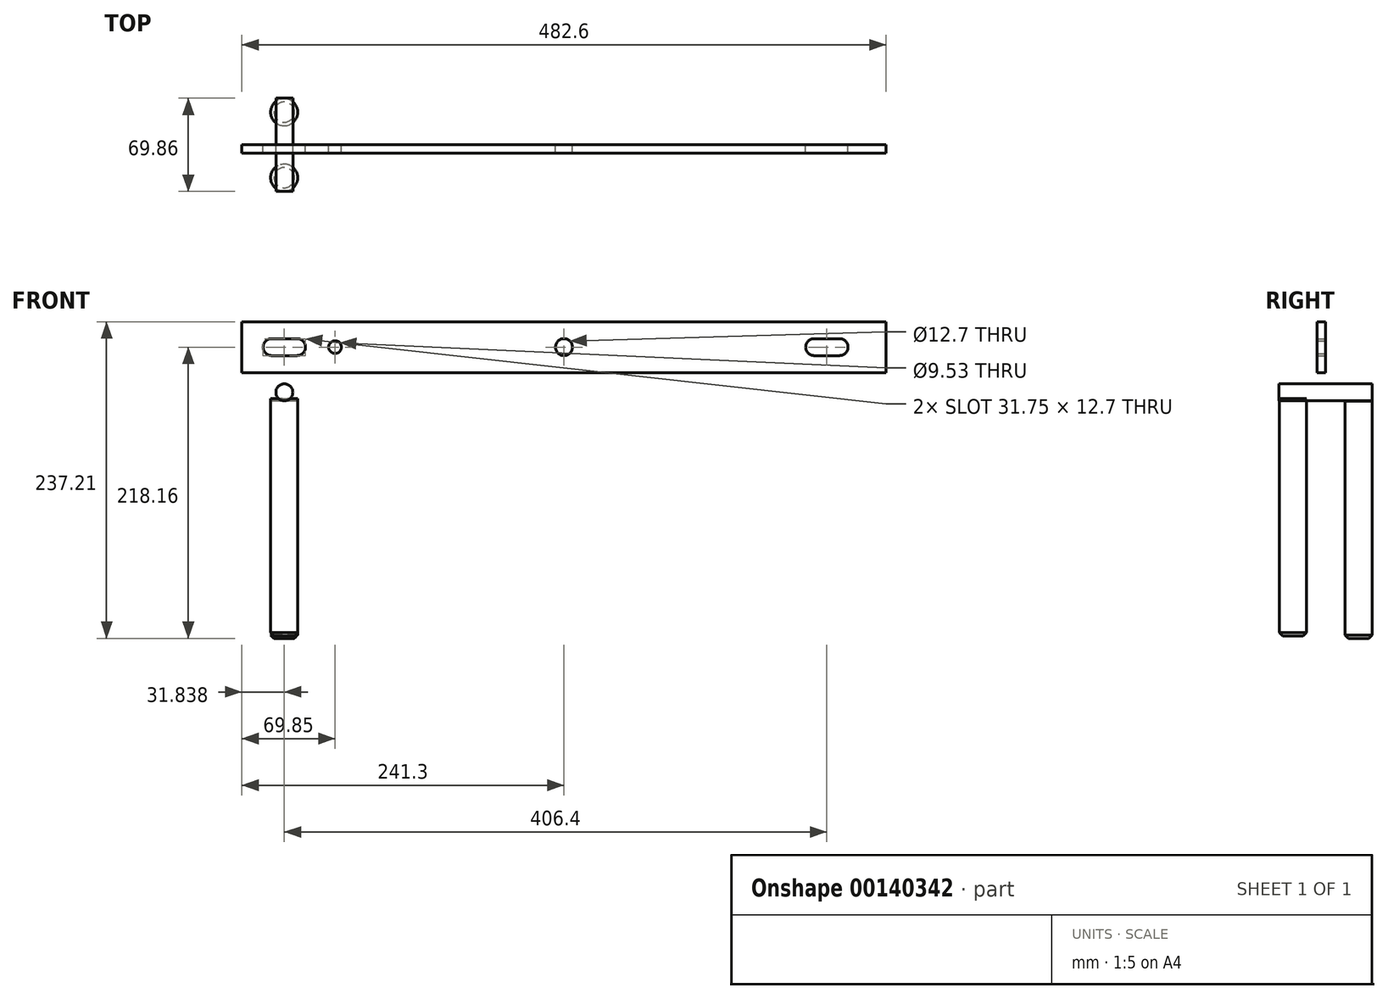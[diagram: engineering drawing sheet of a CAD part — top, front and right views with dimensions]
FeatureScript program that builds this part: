
annotation { "Feature Type Name" : "Feature", "Feature Type Description" : "" }
export const myFeature = defineFeature(function(context is Context, id is Id, definition is map)
    precondition{}
    {
        {
            var Q0;
            Q0=qCreatedBy(makeId("Front.planeOp"),FACE);
            var sketch = newSketch(context, id + "F0", { "sketchPlane" : qUnion([Q0])});
            skLineSegment(sketch, "E0.bottom", {"start": v(-241.3, 19.05) * mm, "end": v(241.3, 19.05) * mm});
            skLineSegment(sketch, "E0.top", {"start": v(-241.3, -19.05) * mm, "end": v(241.3, -19.05) * mm});
            skLineSegment(sketch, "E0.left", {"start": v(-241.3, 19.05) * mm, "end": v(-241.3, -19.05) * mm});
            skLineSegment(sketch, "E0.right", {"start": v(241.3, 19.05) * mm, "end": v(241.3, -19.05) * mm});
            skPoint(sketch, "E0.middle", {"position": v(0, 0) * mm});
            skCircle(sketch, "E1", {"center": v(0, 0) * mm, "radius": 6.35 * mm});
            skCircle(sketch, "E2", {"center": v(-171.45, 0) * mm, "radius": 4.76 * mm});
            skPoint(sketch, "E3", {"position": v(-209.46, 0) * mm});
            skPoint(sketch, "E4", {"position": v(196.94, 0) * mm});
            skPoint(sketch, "E5", {"position": v(-193.59, 0) * mm});
            skPoint(sketch, "E6", {"position": v(-225.34, 0) * mm});
            skPoint(sketch, "E7", {"position": v(212.81, 0) * mm});
            skPoint(sketch, "E8", {"position": v(181.06, 0) * mm});
            skLineSegment(sketch, "E9.bottom", {"start": v(-218.99, 6.35) * mm, "end": v(-199.94, 6.35) * mm});
            skLineSegment(sketch, "E9.top", {"start": v(-218.99, -6.35) * mm, "end": v(-199.94, -6.35) * mm});
            skCircle(sketch, "E10", {"center": v(-218.99, 0) * mm, "radius": 6.35 * mm});
            skCircle(sketch, "E11", {"center": v(-199.94, 0) * mm, "radius": 6.35 * mm});
            skLineSegment(sketch, "E12.bottom", {"start": v(206.46, 6.35) * mm, "end": v(187.41, 6.35) * mm});
            skLineSegment(sketch, "E12.top", {"start": v(206.46, -6.35) * mm, "end": v(187.41, -6.35) * mm});
            skCircle(sketch, "E13", {"center": v(187.41, 0) * mm, "radius": 6.35 * mm});
            skCircle(sketch, "E14", {"center": v(206.46, 0) * mm, "radius": 6.35 * mm});
            skSolve(sketch);
        }
        {
            var Q0;
            Q0=makeQuery(id+"F0.imprint","IMPRINT",FACE,{"disambiguationData":[TD([[makeQuery(id+"F0.imprint","IMPRINT",EDGE,{"derivedFrom":sQuery(id+"F0.wireOp",EDGE,"E0.bottom")}),-1.0]])]});
            extrude(context, id + "F1", {"entities" : qUnion([Q0]), "depth" : 6.35 * mm});
        }
        {
            var Q0;
            Q0=qCreatedBy(makeId("Front.planeOp"),FACE);
            var sketch = newSketch(context, id + "F2", { "sketchPlane" : qUnion([Q0])});
            skCircle(sketch, "E15", {"center": v(-209.45, -33.86) * mm, "radius": 6.35 * mm});
            skSolve(sketch);
        }
        {
            var Q0;
            Q0=makeQuery(id+"F2.imprint","IMPRINT",FACE,{"disambiguationData":[TD([[makeQuery(id+"F2.imprint","IMPRINT",EDGE,{"derivedFrom":sQuery(id+"F2.wireOp",EDGE,"E15")}),1.0]])]});
            extrude(context, id + "F3", {"entities" : qUnion([Q0]), "endBound" : BoundingType.SYMMETRIC, "depth" : 69.85 * mm});
        }
        {
            var Q0;
            Q0=qCreatedBy(makeId("Top.planeOp"),FACE);
            var sketch = newSketch(context, id + "F4", { "sketchPlane" : qUnion([Q0])});
            skLineSegment(sketch, "E16", {"start": v(-209.57, 44.7) * mm, "end": v(-209.57, -47.23) * mm});
            skCircle(sketch, "E17", {"center": v(-209.57, -45.42) * mm, "radius": 10.14 * mm});
            skSolve(sketch);
        }
        {
            var Q0;
            Q0=makeQuery(id+"F4.imprint","IMPRINT",FACE,{"disambiguationData":[TD([[makeQuery(id+"F4.imprint","IMPRINT",EDGE,{"derivedFrom":sQuery(id+"F4.wireOp",EDGE,"E17")}),1.0]])]});
            extrude(context, id + "F5", {"entities" : qUnion([Q0]), "operationType" : NewBodyOperationType.ADD, "oppositeDirection" : true, "depth" : 203.2 * mm, "hasSecondDirection" : true, "secondDirectionOppositeDirection" : true, "secondDirectionDepth" : 25.4 * mm});
        }
        {
            var Q0;
            Q0=makeQuery(id+"F5.opExtrude","SWEPT_BODY",BODY,{"disambiguationData":[OSD([sQuery(id+"F4.wireOp",EDGE,"E17")])]});
            transform(context, id + "F6", {"entities" : qUnion([Q0]), "transformType" : TransformType.TRANSLATION_3D, "dx" : 0 * mm, "dy" : 69.92 * mm, "dz" : -14.96 * mm, "makeCopy" : true});
        }
        {
            var Q0;
            Q0=makeQuery(id+"F5.opExtrude","SWEPT_BODY",BODY,{"disambiguationData":[OSD([sQuery(id+"F4.wireOp",EDGE,"E17")])]});
            transform(context, id + "F7", {"entities" : qUnion([Q0]), "transformType" : TransformType.TRANSLATION_3D, "dx" : 0 * mm, "dy" : 20.86 * mm, "dz" : -13.3 * mm, "makeCopy" : false});
        }
        {
            var Q0;
            Q0=makeQuery(id+"F5.opExtrude","CAP_EDGE",EDGE,{"disambiguationData":[OSD([sQuery(id+"F4.wireOp",EDGE,"E17")])],"isStart":false});
            chamfer(context, id + "F8", {"entities" : qUnion([Q0]), "width" : 2.54 * mm, "tangentPropagation" : true});
        }
        {
            var Q0;
            Q0=makeQuery(id+"F6.opPattern","COPY",EDGE,{"derivedFrom":makeQuery(id+"F5.opExtrude","CAP_EDGE",EDGE,{"disambiguationData":[OSD([sQuery(id+"F4.wireOp",EDGE,"E17")])],"isStart":false}),"instanceName":"1"});
            chamfer(context, id + "F9", {"entities" : qUnion([Q0]), "width" : 2.54 * mm, "tangentPropagation" : true});
        }
    });
